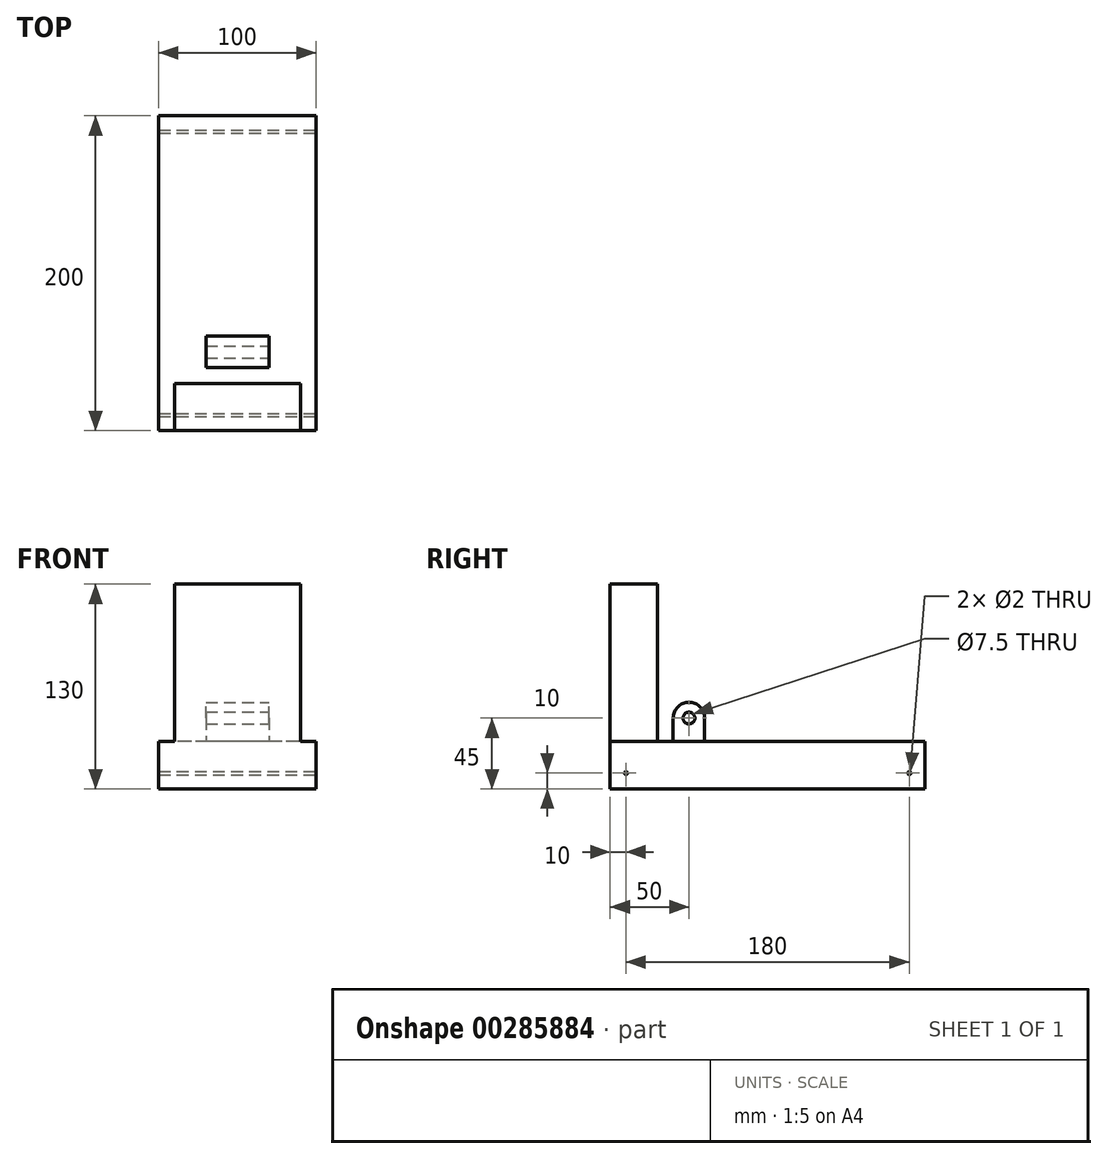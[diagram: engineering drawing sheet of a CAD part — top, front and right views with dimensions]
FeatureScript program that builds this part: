
annotation { "Feature Type Name" : "Feature", "Feature Type Description" : "" }
export const myFeature = defineFeature(function(context is Context, id is Id, definition is map)
    precondition{}
    {
        {
            var Q0;
            Q0=qCreatedBy(makeId("Right.planeOp"),FACE);
            var sketch = newSketch(context, id + "F0", { "sketchPlane" : qUnion([Q0])});
            skLineSegment(sketch, "E0.bottom", {"start": v(100, 15) * mm, "end": v(-100, 15) * mm});
            skLineSegment(sketch, "E0.top", {"start": v(100, -15) * mm, "end": v(-100, -15) * mm});
            skLineSegment(sketch, "E0.left", {"start": v(100, 15) * mm, "end": v(100, -15) * mm});
            skLineSegment(sketch, "E0.right", {"start": v(-100, 15) * mm, "end": v(-100, -15) * mm});
            skPoint(sketch, "E0.middle", {"position": v(0, 0) * mm});
            skSolve(sketch);
        }
        {
            var Q0;
            Q0=makeQuery(id+"F0.imprint","IMPRINT",FACE,{"disambiguationData":[TD([[makeQuery(id+"F0.imprint","IMPRINT",EDGE,{"derivedFrom":sQuery(id+"F0.wireOp",EDGE,"E0.bottom")}),1.0]])]});
            extrude(context, id + "F1", {"entities" : qUnion([Q0]), "endBound" : BoundingType.SYMMETRIC, "depth" : 100 * mm});
        }
        {
            var Q0;
            Q0=makeQuery(id+"F1.opExtrude","SWEPT_FACE",FACE,{"disambiguationData":[OSD([sQuery(id+"F0.wireOp",EDGE,"E0.bottom")])]});
            var sketch = newSketch(context, id + "F2", { "sketchPlane" : qUnion([Q0])});
            skLineSegment(sketch, "E1.bottom", {"start": v(40, -70) * mm, "end": v(-40, -70) * mm});
            skLineSegment(sketch, "E1.top", {"start": v(40, -100) * mm, "end": v(-40, -100) * mm});
            skLineSegment(sketch, "E1.left", {"start": v(40, -70) * mm, "end": v(40, -100) * mm});
            skLineSegment(sketch, "E1.right", {"start": v(-40, -70) * mm, "end": v(-40, -100) * mm});
            skPoint(sketch, "E1.middle", {"position": v(0, -85) * mm});
            skSolve(sketch);
        }
        {
            var Q0;
            Q0=makeQuery(id+"F2.imprint","IMPRINT",FACE,{"disambiguationData":[TD([[makeQuery(id+"F2.imprint","IMPRINT",EDGE,{"derivedFrom":sQuery(id+"F2.wireOp",EDGE,"E1.bottom")}),1.0]])]});
            extrude(context, id + "F3", {"entities" : qUnion([Q0]), "operationType" : NewBodyOperationType.ADD, "depth" : 100 * mm});
        }
        {
            var Q0;
            Q0=makeQuery(id+"F1.opExtrude","SWEPT_FACE",FACE,{"disambiguationData":[OSD([sQuery(id+"F0.wireOp",EDGE,"E0.bottom")])]});
            var sketch = newSketch(context, id + "F4", { "sketchPlane" : qUnion([Q0])});
            skLineSegment(sketch, "E2", {"start": v(-20, -60) * mm, "end": v(-20, -40) * mm});
            skLineSegment(sketch, "E3", {"start": v(-20, -40) * mm, "end": v(20, -40) * mm});
            skLineSegment(sketch, "E4", {"start": v(20, -40) * mm, "end": v(20, -60) * mm});
            skLineSegment(sketch, "E5", {"start": v(20, -60) * mm, "end": v(-20, -60) * mm});
            skLineSegment(sketch, "E6", {"start": v(0, -60) * mm, "end": v(0, -70) * mm});
            skSolve(sketch);
        }
        {
            var Q0;
            {var subQ3=sQuery(id+"F4.wireOp",EDGE,"E2");Q0=makeQuery(id+"F4.imprint","IMPRINT",FACE,{"disambiguationData":[TD([[makeQuery(id+"F4.imprint","IMPRINT",EDGE,{"derivedFrom":subQ3}),-1.0]])]});}
            extrude(context, id + "F5", {"entities" : qUnion([Q0]), "operationType" : NewBodyOperationType.ADD, "depth" : 25 * mm});
        }
        {
            var Q0;
            Q0=makeQuery(id+"F5.opExtrude","SWEPT_FACE",FACE,{"disambiguationData":[OSD([sQuery(id+"F4.wireOp",EDGE,"E4")])]});
            var sketch = newSketch(context, id + "F6", { "sketchPlane" : qUnion([Q0])});
            skCircle(sketch, "E7", {"center": v(-50, 30) * mm, "radius": 3.75 * mm});
            skSolve(sketch);
        }
        {
            var Q0;
            Q0=makeQuery(id+"F6.imprint","IMPRINT",FACE,{"disambiguationData":[TD([[makeQuery(id+"F6.imprint","IMPRINT",EDGE,{"derivedFrom":sQuery(id+"F6.wireOp",EDGE,"E7")}),1.0]])]});
            extrude(context, id + "F7", {"entities" : qUnion([Q0]), "operationType" : NewBodyOperationType.REMOVE, "endBound" : BoundingType.THROUGH_ALL, "oppositeDirection" : true, "depth" : 25 * mm});
        }
        {
            var Q0;
            Q0=makeQuery(id+"F5.opExtrude","CAP_EDGE",EDGE,{"disambiguationData":[OSD([sQuery(id+"F4.wireOp",EDGE,"E3")])],"isStart":false});
            var Q1;
            Q1=makeQuery(id+"F5.opExtrude","CAP_EDGE",EDGE,{"disambiguationData":[OSD([sQuery(id+"F4.wireOp",EDGE,"E5")])],"isStart":false});
            fillet(context, id + "F8", {"entities" : qUnion([Q0, Q1]), "radius" : 10 * mm, "tangentPropagation" : true, "allowEdgeOverflow" : false});
        }
        {
            var Q0;
            Q0=makeQuery(id+"F1.opExtrude","CAP_FACE",FACE,{"disambiguationData":[OSD([sQuery(id+"F0.wireOp",EDGE,"E0.bottom"),sQuery(id+"F0.wireOp",EDGE,"E0.top"),sQuery(id+"F0.wireOp",EDGE,"E0.left"),sQuery(id+"F0.wireOp",EDGE,"E0.right")])],"isStart":false});
            var sketch = newSketch(context, id + "F9", { "sketchPlane" : qUnion([Q0])});
            skCircle(sketch, "E8", {"center": v(-90, -5) * mm, "radius": 1 * mm});
            skCircle(sketch, "E9", {"center": v(90, -5) * mm, "radius": 1 * mm});
            skSolve(sketch);
        }
        {
            var Q0;
            Q0=makeQuery(id+"F9.imprint","IMPRINT",FACE,{"disambiguationData":[TD([[makeQuery(id+"F9.imprint","IMPRINT",EDGE,{"derivedFrom":sQuery(id+"F9.wireOp",EDGE,"E9")}),1.0]])]});
            var Q1;
            Q1=makeQuery(id+"F9.imprint","IMPRINT",FACE,{"disambiguationData":[TD([[makeQuery(id+"F9.imprint","IMPRINT",EDGE,{"derivedFrom":sQuery(id+"F9.wireOp",EDGE,"E8")}),1.0]])]});
            extrude(context, id + "F10", {"entities" : qUnion([Q0, Q1]), "operationType" : NewBodyOperationType.REMOVE, "endBound" : BoundingType.THROUGH_ALL, "oppositeDirection" : true, "depth" : 25 * mm});
        }
    });
